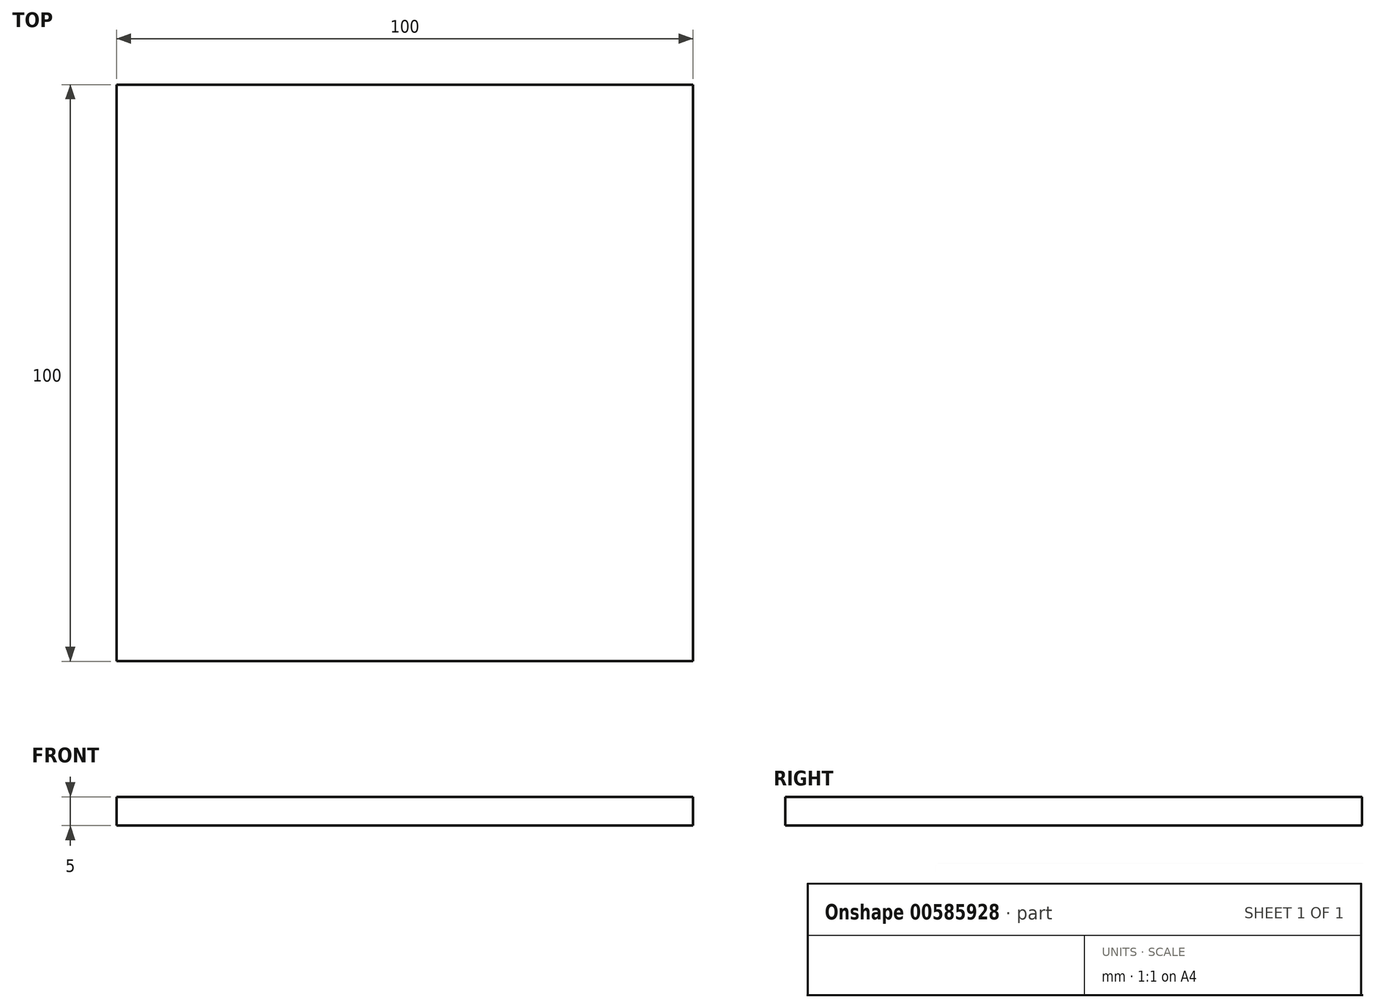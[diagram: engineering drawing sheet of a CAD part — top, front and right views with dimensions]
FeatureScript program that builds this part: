
annotation { "Feature Type Name" : "Feature", "Feature Type Description" : "" }
export const myFeature = defineFeature(function(context is Context, id is Id, definition is map)
    precondition{}
    {
        {
            var Q0;
            Q0=qCreatedBy(makeId("Top.planeOp"),FACE);
            var sketch = newSketch(context, id + "F0", { "sketchPlane" : qUnion([Q0])});
            skLineSegment(sketch, "E0", {"start": v(-53.14, -50.72) * mm, "end": v(46.86, -50.72) * mm});
            skLineSegment(sketch, "E1", {"start": v(46.86, -50.72) * mm, "end": v(46.86, 49.28) * mm});
            skLineSegment(sketch, "E2", {"start": v(46.86, 49.28) * mm, "end": v(-53.14, 49.28) * mm});
            skLineSegment(sketch, "E3", {"start": v(-53.14, 49.28) * mm, "end": v(-53.14, -50.72) * mm});
            skSolve(sketch);
        }
        {
            var Q0;
            Q0 = qSketchRegion(id + "F0", true);
            extrude(context, id + "F1", {"entities" : qUnion([Q0]), "depth" : 5 * mm, "offsetDistance" : 25 * mm});
        }
    });
